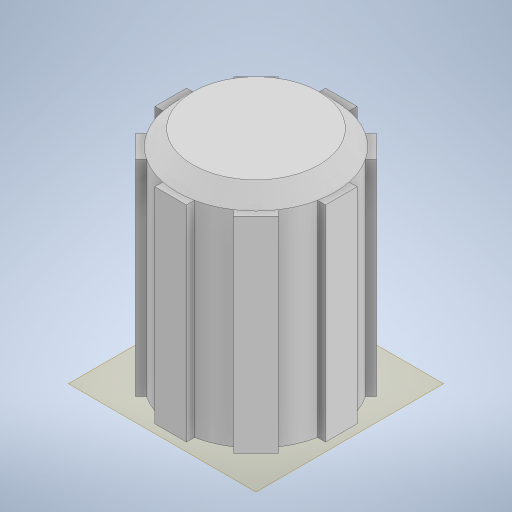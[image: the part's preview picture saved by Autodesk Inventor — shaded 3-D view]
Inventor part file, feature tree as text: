
AUTODESK INVENTOR PART (.ipt)
format: ipt  version: 2023 (Build 270158000, 158)  size: 268,800 bytes
history: native  units: mm
features: extrude x3, sketch x3, chamfer x2, pattern_circular x1
ambient origin geometry x8: Origin, YZ Plane, XZ Plane, XY Plane, X Axis, Y Axis, Z Axis, Center Point
bodies: Solid1 (feature_tree)
feature tree (9):
  extrude  "Extrusion1"  Depth=4.5mm
  extrude  "Extrusion2"  Depth=10.0mm TaperAngle=0.0deg
  chamfer  "Chamfer1"  Distance=2.0mm
  extrude  "Extrusion3"  Depth=0.5mm
  pattern_circular  "Circular Pattern1"  [2 undecoded]
  chamfer  "Chamfer2"  Distance=1.0mm
  sketch  "Sketch1"  dims[d0=6.0mm d1=4.5mm]
  sketch  "Sketch2"  dims[d2=10.0mm d3=12.0mm d4=0.0mm d5=2.0mm d6=0.0mm]
  sketch  "Sketch3"  dims[d7=1.0mm d8=2.0mm d9=45.0deg d10=2.0mm d11=0.5mm d12=1.0mm d13=13.0mm d14=0.0mm d15=80.0mm d16=360.0deg d18=1.0mm d19=2.0mm d20=45.0deg]
note: 2 required parameter values undecoded (feature->parameter linkage not recoverable at this tier; creation-order binding heuristic only, values carry confidence <= 0.55)
